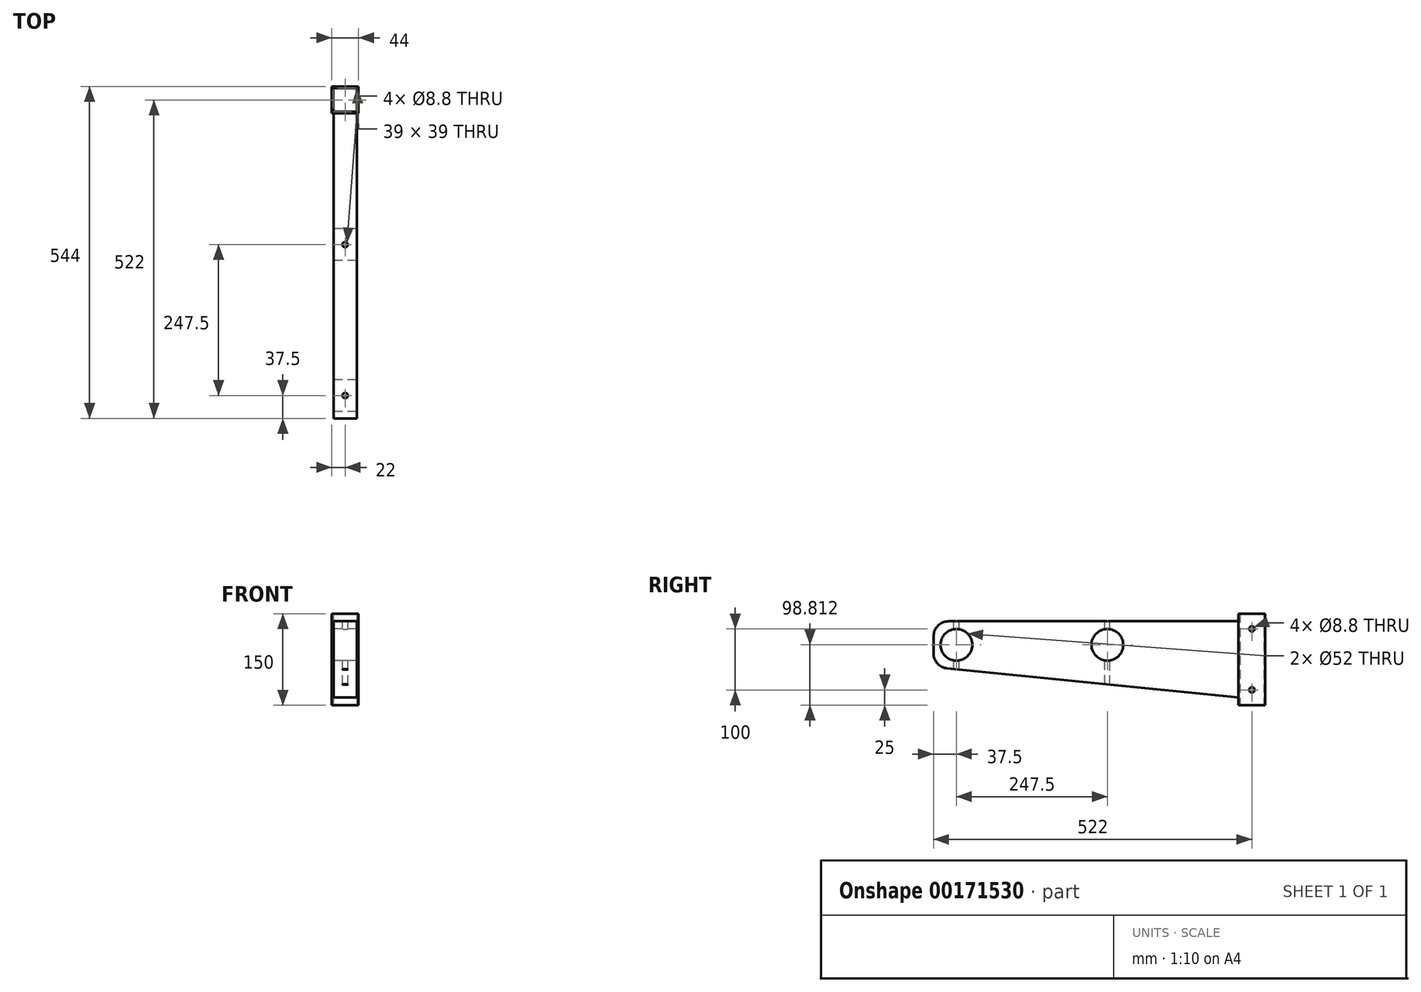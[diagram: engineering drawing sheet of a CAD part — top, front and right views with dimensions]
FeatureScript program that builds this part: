
annotation { "Feature Type Name" : "Feature", "Feature Type Description" : "" }
export const myFeature = defineFeature(function(context is Context, id is Id, definition is map)
    precondition{}
    {
        {
            var Q0;
            Q0=qCreatedBy(makeId("Top.planeOp"),FACE);
            var sketch = newSketch(context, id + "F0", { "sketchPlane" : qUnion([Q0])});
            skLineSegment(sketch, "E0.bottom", {"start": v(22, -22) * mm, "end": v(-22, -22) * mm});
            skLineSegment(sketch, "E0.top", {"start": v(22, 22) * mm, "end": v(-22, 22) * mm});
            skLineSegment(sketch, "E0.left", {"start": v(22, -22) * mm, "end": v(22, 22) * mm});
            skLineSegment(sketch, "E0.right", {"start": v(-22, -22) * mm, "end": v(-22, 22) * mm});
            skPoint(sketch, "E0.middle", {"position": v(0, 0) * mm});
            skLineSegment(sketch, "E1.bottom", {"start": v(19.5, -19.5) * mm, "end": v(-19.5, -19.5) * mm});
            skLineSegment(sketch, "E1.top", {"start": v(19.5, 19.5) * mm, "end": v(-19.5, 19.5) * mm});
            skLineSegment(sketch, "E1.left", {"start": v(19.5, -19.5) * mm, "end": v(19.5, 19.5) * mm});
            skLineSegment(sketch, "E1.right", {"start": v(-19.5, -19.5) * mm, "end": v(-19.5, 19.5) * mm});
            skSolve(sketch);
        }
        {
            var Q0;
            Q0=makeQuery(id+"F0.imprint","IMPRINT",FACE,{"disambiguationData":[TD([[makeQuery(id+"F0.imprint","IMPRINT",EDGE,{"derivedFrom":sQuery(id+"F0.wireOp",EDGE,"E0.bottom")}),-1.0]])]});
            extrude(context, id + "F1", {"entities" : qUnion([Q0]), "depth" : 150 * mm});
        }
        {
            var Q0;
            Q0=makeQuery(id+"F1.opExtrude","SWEPT_FACE",FACE,{"disambiguationData":[OSD([sQuery(id+"F0.wireOp",EDGE,"E0.right")])]});
            var sketch = newSketch(context, id + "F2", { "sketchPlane" : qUnion([Q0])});
            skPoint(sketch, "E2", {"position": v(0, 25) * mm});
            skPoint(sketch, "E2.positionSnap0", {"position": v(0, 0) * mm});
            skPoint(sketch, "E3", {"position": v(0, 125) * mm});
            skPoint(sketch, "E3.positionSnap0", {"position": v(0, 150) * mm});
            skSolve(sketch);
        }
        {
            var Q0;
            Q0=sQuery(id+"F2.wireOp",VERTEX,"E3");
            var Q1;
            Q1=sQuery(id+"F2.wireOp",VERTEX,"E2");
            var Q2;
            Q2=makeQuery(id+"F1.opExtrude","SWEPT_BODY",BODY,{"disambiguationData":[OSD([sQuery(id+"F0.wireOp",EDGE,"E0.bottom"),sQuery(id+"F0.wireOp",EDGE,"E0.top"),sQuery(id+"F0.wireOp",EDGE,"E0.left"),sQuery(id+"F0.wireOp",EDGE,"E0.right"),sQuery(id+"F0.wireOp",EDGE,"E1.bottom"),sQuery(id+"F0.wireOp",EDGE,"E1.top"),sQuery(id+"F0.wireOp",EDGE,"E1.left"),sQuery(id+"F0.wireOp",EDGE,"E1.right")])]});
            hole(context, id + "F3", {"style" : HoleStyle.SIMPLE, "endStyle" : HoleEndStyle.THROUGH, "standardTappedOrClearance" : lookupTablePath({ "standard" : "ISO", "fit" : "Normal", "size" : "M8", "type" : "Clearance" }), "standardBlindInLast" : lookupTablePath({ "fit" : "Standard", "standard" : "ISO", "size" : "M8", "type" : "Clearance" }), "holeDiameter" : 8.8 * mm, "locations" : qUnion([Q0, Q1]), "scope" : qUnion([Q2]), "isTappedThrough" : true});
        }
        {
            var Q0;
            Q0=qCreatedBy(makeId("Right.planeOp"),FACE);
            var sketch = newSketch(context, id + "F4", { "sketchPlane" : qUnion([Q0])});
            skLineSegment(sketch, "E4", {"start": v(-22, 137.5) * mm, "end": v(-522, 137.5) * mm});
            skLineSegment(sketch, "E5", {"start": v(-522, 137.5) * mm, "end": v(-522, 62.5) * mm});
            skLineSegment(sketch, "E6", {"start": v(-522, 62.5) * mm, "end": v(-22, 12.5) * mm});
            skLineSegment(sketch, "E7", {"start": v(-22, 137.5) * mm, "end": v(-22, 12.5) * mm});
            skSolve(sketch);
        }
        {
            var Q0;
            Q0=makeQuery(id+"F4.imprint","IMPRINT",FACE,{"disambiguationData":[TD([[makeQuery(id+"F4.imprint","IMPRINT",EDGE,{"derivedFrom":sQuery(id+"F4.wireOp",EDGE,"E4")}),1.0]])]});
            extrude(context, id + "F5", {"entities" : qUnion([Q0]), "operationType" : NewBodyOperationType.ADD, "endBound" : BoundingType.SYMMETRIC, "depth" : 38 * mm});
        }
        {
            var Q0;
            Q0=makeQuery(id+"F5.opExtrude","SWEPT_EDGE",EDGE,{"disambiguationData":[OSD([sQuery(id+"F4.wireOp",EDGE,"E4"),sQuery(id+"F4.wireOp",EDGE,"E5")])]});
            var Q1;
            Q1=makeQuery(id+"F5.opExtrude","SWEPT_EDGE",EDGE,{"disambiguationData":[OSD([sQuery(id+"F4.wireOp",EDGE,"E5"),sQuery(id+"F4.wireOp",EDGE,"E6")])]});
            fillet(context, id + "F6", {"entities" : qUnion([Q0, Q1]), "radius" : 25 * mm, "tangentPropagation" : true, "allowEdgeOverflow" : false});
        }
        {
            var Q0;
            Q0=makeQuery(id+"F5.opExtrude","CAP_FACE",FACE,{"disambiguationData":[OSD([sQuery(id+"F4.wireOp",EDGE,"E4"),sQuery(id+"F4.wireOp",EDGE,"E5"),sQuery(id+"F4.wireOp",EDGE,"E6"),sQuery(id+"F4.wireOp",EDGE,"E7")])],"isStart":true});
            var sketch = newSketch(context, id + "F7", { "sketchPlane" : qUnion([Q0])});
            skPoint(sketch, "E8", {"position": v(484.5, 98.81) * mm});
            skPoint(sketch, "E8.positionSnap0", {"position": v(522, 98.81) * mm});
            skPoint(sketch, "E9", {"position": v(237, 98.81) * mm});
            skSolve(sketch);
        }
        {
            var Q0;
            Q0=sQuery(id+"F7.wireOp",VERTEX,"E8");
            var Q1;
            Q1=sQuery(id+"F7.wireOp",VERTEX,"E9");
            var Q2;
            Q2=makeQuery(id+"F1.opExtrude","SWEPT_BODY",BODY,{"disambiguationData":[OSD([sQuery(id+"F0.wireOp",EDGE,"E0.bottom"),sQuery(id+"F0.wireOp",EDGE,"E0.top"),sQuery(id+"F0.wireOp",EDGE,"E0.left"),sQuery(id+"F0.wireOp",EDGE,"E0.right"),sQuery(id+"F0.wireOp",EDGE,"E1.bottom"),sQuery(id+"F0.wireOp",EDGE,"E1.top"),sQuery(id+"F0.wireOp",EDGE,"E1.left"),sQuery(id+"F0.wireOp",EDGE,"E1.right")])]});
            hole(context, id + "F8", {"style" : HoleStyle.SIMPLE, "endStyle" : HoleEndStyle.THROUGH, "holeDiameter" : 52 * mm, "locations" : qUnion([Q0, Q1]), "scope" : qUnion([Q2]), "isTappedThrough" : true});
        }
        {
            var Q0;
            Q0=makeQuery(id+"F5.opExtrude","SWEPT_FACE",FACE,{"disambiguationData":[OSD([sQuery(id+"F4.wireOp",EDGE,"E4")])]});
            var sketch = newSketch(context, id + "F9", { "sketchPlane" : qUnion([Q0])});
            skPoint(sketch, "E10", {"position": v(0, -484.5) * mm});
            skPoint(sketch, "E10.positionSnap0", {"position": v(0, -497) * mm});
            skPoint(sketch, "E11", {"position": v(0, -237) * mm});
            skSolve(sketch);
        }
        {
            var Q0;
            Q0=sQuery(id+"F9.wireOp",VERTEX,"E11");
            var Q1;
            Q1=sQuery(id+"F9.wireOp",VERTEX,"E10");
            var Q2;
            Q2=makeQuery(id+"F1.opExtrude","SWEPT_BODY",BODY,{"disambiguationData":[OSD([sQuery(id+"F0.wireOp",EDGE,"E0.bottom"),sQuery(id+"F0.wireOp",EDGE,"E0.top"),sQuery(id+"F0.wireOp",EDGE,"E0.left"),sQuery(id+"F0.wireOp",EDGE,"E0.right"),sQuery(id+"F0.wireOp",EDGE,"E1.bottom"),sQuery(id+"F0.wireOp",EDGE,"E1.top"),sQuery(id+"F0.wireOp",EDGE,"E1.left"),sQuery(id+"F0.wireOp",EDGE,"E1.right")])]});
            hole(context, id + "F10", {"style" : HoleStyle.SIMPLE, "endStyle" : HoleEndStyle.THROUGH, "standardTappedOrClearance" : lookupTablePath({ "standard" : "ISO", "fit" : "Normal", "size" : "M8", "type" : "Clearance" }), "standardBlindInLast" : lookupTablePath({ "fit" : "Standard", "standard" : "ISO", "size" : "M8", "type" : "Clearance" }), "holeDiameter" : 8.8 * mm, "locations" : qUnion([Q0, Q1]), "scope" : qUnion([Q2]), "isTappedThrough" : true});
        }
    });
